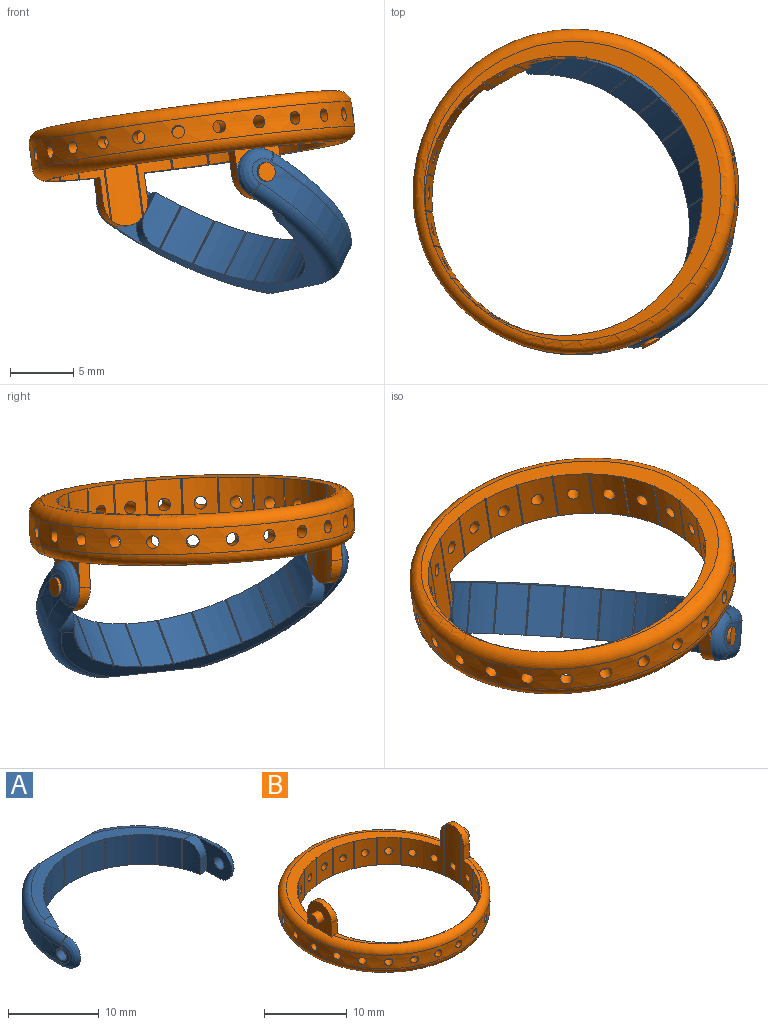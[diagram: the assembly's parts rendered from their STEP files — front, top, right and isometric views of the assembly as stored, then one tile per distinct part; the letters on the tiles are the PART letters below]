
ASSEMBLY  parts=2 mates=1
PART A: 58 faces, bbox 27.8x16x4.1 mm
  f0: cylinder r=12.8mm len=13.16mm, axis (0,0,-1), area 29mm2, adj f7,f51,f52,f53,f54,f55,f57
  f1: cylinder r=12.8mm len=13.16mm, axis (0,0,-1), area 29mm2, adj f7,f46,f47,f48,f49,f50,f56
  f2: plane 1.37x0.02mm, normal (0,0,1), area 0mm2, adj f6,f51
  f3: plane 22.72x8mm, normal (0,0,1), area 37mm2, adj f7,f10,f11,f12,f13,f14,f15,f16
  f4: plane 1.37x0.02mm, normal (0,0,-1), area 0mm2, adj f8,f50
  f5: plane 23.48x10mm, normal (0,0,-1), area 41.1mm2, adj f7,f9,f10,f11,f12,f13,f14,f15
  f6: plane 5.67x4.1mm, normal (-1,0,0), area 13.3mm2, adj f2,f41,f43,f44,f51,f52,f53,f54
  f7: plane 12.39x4mm, normal (0,1,0), area 47.7mm2, adj f0,f1,f3,f5,f46,f50,f51,f52
  f8: plane 5.67x4.1mm, normal (1,0,0), area 13.3mm2, adj f4,f9,f42,f45,f46,f47,f48,f49
  f9: plane 2x0.96mm, normal (0,-1,0), area 1.9mm2, adj f5,f8,f10,f45,f50
  f10: cylinder r=11mm len=4mm, axis (0,0,-1), area 8.1mm2, adj f3,f5,f9,f11,f45
  f11: plane 4x0.09mm, normal (0.78,0.62,0), area 0.5mm2, adj f3,f5,f10,f12
  f12: plane 4x0.11mm, normal (0.12,-0.99,0), area 0.5mm2, adj f3,f5,f11,f13
  f13: cylinder r=11mm len=4mm, axis (0,0,-1), area 11.1mm2, adj f3,f5,f12,f14
  f14: plane 4x0.11mm, normal (0.92,0.4,0), area 0.5mm2, adj f3,f5,f13,f15
  f15: plane 4x0.11mm, normal (-0.15,-0.99,0), area 0.5mm2, adj f3,f5,f14,f16
  f16: cylinder r=11mm len=4mm, axis (0,0,-1), area 11.1mm2, adj f3,f5,f15,f17
  f17: plane 4x0.11mm, normal (0.99,0.15,0), area 0.5mm2, adj f3,f5,f16,f18
  f18: plane 4x0.11mm, normal (-0.4,-0.92,0), area 0.5mm2, adj f3,f5,f17,f19
  f19: cylinder r=11mm len=4mm, axis (0,0,-1), area 11.1mm2, adj f3,f5,f18,f20
  f20: plane 4x0.11mm, normal (0.99,-0.12,0), area 0.5mm2, adj f3,f5,f19,f21
  f21: plane 4x0.09mm, normal (-0.62,-0.78,0), area 0.5mm2, adj f3,f5,f20,f22
  f22: cylinder r=11mm len=4mm, axis (0,0,-1), area 11.1mm2, adj f3,f5,f21,f23
  f23: plane 4x0.11mm, normal (0.93,-0.37,0), area 0.5mm2, adj f3,f5,f22,f24
  f24: plane 4x0.09mm, normal (-0.8,-0.6,0), area 0.5mm2, adj f3,f5,f23,f25
  f25: cylinder r=11mm len=4mm, axis (0,0,-1), area 11.1mm2, adj f3,f5,f24,f26
  f26: plane 4x0.09mm, normal (0.8,-0.6,0), area 0.5mm2, adj f3,f5,f25,f27
  f27: plane 4x0.11mm, normal (-0.93,-0.37,0), area 0.5mm2, adj f3,f5,f26,f28
  f28: cylinder r=11mm len=4mm, axis (0,0,-1), area 11.1mm2, adj f3,f5,f27,f29
  f29: plane 4x0.09mm, normal (0.62,-0.78,0), area 0.5mm2, adj f3,f5,f28,f30
  f30: plane 4x0.11mm, normal (-0.99,-0.12,0), area 0.5mm2, adj f3,f5,f29,f31
  f31: cylinder r=11mm len=4mm, axis (0,0,-1), area 11.1mm2, adj f3,f5,f30,f32
  f32: plane 4x0.11mm, normal (0.4,-0.92,0), area 0.5mm2, adj f3,f5,f31,f33
  f33: plane 4x0.11mm, normal (-0.99,0.15,0), area 0.5mm2, adj f3,f5,f32,f34
  f34: cylinder r=11mm len=4mm, axis (0,0,-1), area 11.1mm2, adj f3,f5,f33,f35
  f35: plane 4x0.11mm, normal (0.15,-0.99,0), area 0.5mm2, adj f3,f5,f34,f36
  f36: plane 4x0.11mm, normal (-0.92,0.4,0), area 0.5mm2, adj f3,f5,f35,f37
  f37: cylinder r=11mm len=4mm, axis (0,0,-1), area 11.1mm2, adj f3,f5,f36,f38
  f38: plane 4x0.11mm, normal (-0.12,-0.99,0), area 0.5mm2, adj f3,f5,f37,f39
  f39: plane 4x0.09mm, normal (-0.78,0.62,0), area 0.5mm2, adj f3,f5,f38,f40
  f40: cylinder r=11mm len=4mm, axis (0,0,-1), area 8.1mm2, adj f3,f5,f39,f41,f44
  f41: plane 2x0.96mm, normal (0,-1,0), area 1.9mm2, adj f5,f6,f40,f44,f52
  f42: plane 1.37x0.02mm, normal (0,0,1), area 0mm2, adj f8,f46
  f43: plane 1.37x0.02mm, normal (0,0,-1), area 0mm2, adj f6,f52
  f44: cylinder r=2mm len=2mm, axis (-1,0,0), area 3.5mm2, adj f3,f6,f40,f41,f51
  f45: cylinder r=2mm len=2mm, axis (-1,0,0), area 3.5mm2, adj f3,f8,f9,f10,f46
  f46: torus R=11.8mm, axis (0,0,1), area 22.7mm2, adj f1,f3,f7,f8,f42,f45,f47
  f47: bspline ~1.12x1.02mm, area 0.2mm2, adj f1,f8,f46,f48
  f48: bspline ~4x2mm, area 7.2mm2, adj f1,f8,f47,f49
  f49: bspline ~1.12x1.02mm, area 0.2mm2, adj f1,f8,f48,f50
  f50: torus R=11.8mm, axis (0,0,1), area 23.1mm2, adj f1,f4,f5,f7,f8,f9,f49
  f51: torus R=11.8mm, axis (0,0,1), area 22.7mm2, adj f0,f2,f3,f6,f7,f44,f53
  f52: torus R=11.8mm, axis (0,0,1), area 23.1mm2, adj f0,f5,f6,f7,f41,f43,f54
  f53: bspline ~1.12x1.02mm, area 0.2mm2, adj f0,f6,f51,f55
  f54: bspline ~1.12x1.02mm, area 0.2mm2, adj f0,f6,f52,f55
  f55: bspline ~4x2mm, area 7.2mm2, adj f0,f6,f53,f54
  f56: cylinder r=0.75mm len=1.5mm, axis (1,0,0), area 4.6mm2, adj f1,f8
  f57: cylinder r=0.75mm len=1.5mm, axis (1,0,0), area 4.6mm2, adj f0,f6
PART B: 125 faces, bbox 27.7x27.7x8 mm
  f0: plane 2.72x0.72mm, normal (0,0,1), area 0.1mm2, adj f44,f45,f46,f124
  f1: plane 8.21x7.21mm, normal (0,0,1), area 3.4mm2, adj f33,f34,f35,f36,f37,f38,f39,f40
  f2: plane 1.37x0.02mm, normal (0,0,1), area 0mm2, adj f112,f124
  f3: plane 23.48x10.6mm, normal (0,0,1), area 44.1mm2, adj f12,f13,f14,f15,f16,f17,f18,f19
  f4: plane 1.37x0.02mm, normal (0,0,1), area 0mm2, adj f115,f124
  f5: plane 8.21x7.21mm, normal (0,0,1), area 3.4mm2, adj f53,f54,f55,f56,f57,f58,f59,f60
  f6: plane 2.72x0.72mm, normal (0,0,1), area 0.1mm2, adj f50,f51,f52,f124
  f7: plane 1.38x0.09mm, normal (0,0,1), area 0mm2, adj f48,f49,f124
  f8: plane 1.38x0.09mm, normal (0,0,-1), area 0mm2, adj f47,f48,f123
  f9: plane 1.38x0.09mm, normal (0,0,-1), area 0mm2, adj f48,f49,f123
  f10: plane 2.72x0.72mm, normal (0,0,-1), area 0.1mm2, adj f50,f51,f52,f123
  f11: plane 23.6x22.81mm, normal (0,0,-1), area 57mm2, adj f12,f13,f14,f15,f16,f17,f18,f19
  f12: cylinder r=11mm len=4mm, axis (0,0,-1), area 10.3mm2, adj f3,f11,f13,f84,f87
  f13: plane 4x0.09mm, normal (0.8,-0.6,0), area 0.5mm2, adj f3,f11,f12,f14
  f14: plane 4x0.11mm, normal (-0.93,-0.37,0), area 0.5mm2, adj f3,f11,f13,f15
  f15: cylinder r=11mm len=4mm, axis (0,0,-1), area 10.3mm2, adj f3,f11,f14,f16,f94
  f16: plane 4x0.09mm, normal (0.62,-0.78,0), area 0.5mm2, adj f3,f11,f15,f17
  f17: plane 4x0.11mm, normal (-0.99,-0.12,0), area 0.5mm2, adj f3,f11,f16,f18
  f18: cylinder r=11mm len=4mm, axis (0,0,-1), area 10.3mm2, adj f3,f11,f17,f19,f92
  f19: plane 4x0.11mm, normal (0.4,-0.92,0), area 0.5mm2, adj f3,f11,f18,f20
  f20: plane 4x0.11mm, normal (-0.99,0.15,0), area 0.5mm2, adj f3,f11,f19,f21
  f21: cylinder r=11mm len=4mm, axis (0,0,-1), area 10.3mm2, adj f3,f11,f20,f22,f93
  f22: plane 4x0.11mm, normal (0.15,-0.99,0), area 0.5mm2, adj f3,f11,f21,f23
  f23: plane 4x0.11mm, normal (-0.92,0.4,0), area 0.5mm2, adj f3,f11,f22,f24
  f24: cylinder r=11mm len=4mm, axis (0,0,-1), area 10.3mm2, adj f3,f11,f23,f25,f91
  f25: plane 4x0.11mm, normal (-0.12,-0.99,0), area 0.5mm2, adj f3,f11,f24,f26
  f26: plane 4x0.09mm, normal (-0.78,0.62,0), area 0.5mm2, adj f3,f11,f25,f27
  f27: cylinder r=11mm len=7.33mm, axis (0,0,-1), area 11.8mm2, adj f3,f11,f26,f28,f90,f113,f121
  f28: plane 7.38x0.11mm, normal (-0.37,-0.93,0), area 0.8mm2, adj f11,f27,f29,f121
  f29: plane 7.45x0.09mm, normal (-0.6,0.8,0), area 0.9mm2, adj f11,f28,f30,f121
  f30: cylinder r=11mm len=8mm, axis (0,0,-1), area 20.9mm2, adj f11,f29,f31,f89,f121
  f31: plane 7.45x0.09mm, normal (-0.6,-0.8,0), area 0.9mm2, adj f11,f30,f32,f121
  f32: plane 7.38x0.11mm, normal (-0.37,0.93,0), area 0.8mm2, adj f11,f31,f33,f121
  f33: cylinder r=11mm len=7.33mm, axis (0,0,-1), area 11.8mm2, adj f1,f11,f32,f34,f88,f111,f121
  f34: plane 4x0.09mm, normal (-0.78,-0.62,0), area 0.5mm2, adj f1,f11,f33,f35
  f35: plane 4x0.11mm, normal (-0.12,0.99,0), area 0.5mm2, adj f1,f11,f34,f36
  f36: cylinder r=11mm len=4mm, axis (0,0,-1), area 10.3mm2, adj f1,f11,f35,f37,f108
  f37: plane 4x0.11mm, normal (-0.92,-0.4,0), area 0.5mm2, adj f1,f11,f36,f38
  f38: plane 4x0.11mm, normal (0.15,0.99,0), area 0.5mm2, adj f1,f11,f37,f39
  f39: cylinder r=11mm len=4mm, axis (0,0,-1), area 10.3mm2, adj f1,f11,f38,f40,f107
  f40: plane 4x0.11mm, normal (-0.99,-0.15,0), area 0.5mm2, adj f1,f11,f39,f41
  f41: plane 4x0.11mm, normal (0.4,0.92,0), area 0.5mm2, adj f1,f11,f40,f42
  f42: cylinder r=11mm len=4mm, axis (0,0,-1), area 10.3mm2, adj f1,f11,f41,f43,f109
  f43: plane 4x0.11mm, normal (-0.99,0.12,0), area 0.5mm2, adj f1,f11,f42,f44,f123,f124
  f44: plane 4x0.09mm, normal (0.62,0.78,0), area 0.5mm2, adj f0,f43,f45,f86,f123,f124
  f45: cylinder r=11mm len=4mm, axis (0,0,-1), area 10.3mm2, adj f0,f44,f46,f86,f110
  f46: plane 4x0.11mm, normal (-0.93,0.37,0), area 0.5mm2, adj f0,f45,f47,f86,f123,f124
  f47: plane 4x0.09mm, normal (0.8,0.6,0), area 0.5mm2, adj f8,f46,f48,f85,f123,f124
  f48: cylinder r=11mm len=4mm, axis (0,0,-1), area 10.3mm2, adj f7,f8,f9,f47,f49,f85,f106
  f49: plane 4x0.09mm, normal (-0.8,0.6,0), area 0.5mm2, adj f7,f9,f48,f50,f123,f124
  f50: plane 4x0.11mm, normal (0.93,0.37,0), area 0.5mm2, adj f6,f10,f49,f51,f123,f124
  f51: cylinder r=11mm len=4mm, axis (0,0,-1), area 10.3mm2, adj f6,f10,f50,f52,f105
  f52: plane 4x0.09mm, normal (-0.62,0.78,0), area 0.5mm2, adj f6,f10,f51,f53,f123,f124
  f53: plane 4x0.11mm, normal (0.99,0.12,0), area 0.5mm2, adj f5,f11,f52,f54,f123,f124
  f54: cylinder r=11mm len=4mm, axis (0,0,-1), area 10.3mm2, adj f5,f11,f53,f55,f103
  f55: plane 4x0.11mm, normal (-0.4,0.92,0), area 0.5mm2, adj f5,f11,f54,f56
  f56: plane 4x0.11mm, normal (0.99,-0.15,0), area 0.5mm2, adj f5,f11,f55,f57
  f57: cylinder r=11mm len=4mm, axis (0,0,-1), area 10.3mm2, adj f5,f11,f56,f58,f104
  f58: plane 4x0.11mm, normal (-0.15,0.99,0), area 0.5mm2, adj f5,f11,f57,f59
  f59: plane 4x0.11mm, normal (0.92,-0.4,0), area 0.5mm2, adj f5,f11,f58,f60
  f60: cylinder r=11mm len=4mm, axis (0,0,-1), area 10.3mm2, adj f5,f11,f59,f61,f102
  f61: plane 4x0.11mm, normal (0.12,0.99,0), area 0.5mm2, adj f5,f11,f60,f62
  f62: plane 4x0.09mm, normal (0.78,-0.62,0), area 0.5mm2, adj f5,f11,f61,f63
  f63: cylinder r=11mm len=7.33mm, axis (0,0,-1), area 11.8mm2, adj f5,f11,f62,f64,f101,f116,f122
  f64: plane 7.38x0.11mm, normal (0.37,0.93,0), area 0.8mm2, adj f11,f63,f65,f122
  f65: plane 7.45x0.09mm, normal (0.6,-0.8,0), area 0.9mm2, adj f11,f64,f66,f122
  f66: cylinder r=11mm len=8mm, axis (0,0,-1), area 20.9mm2, adj f11,f65,f67,f100,f122
  f67: plane 7.45x0.09mm, normal (0.6,0.8,0), area 0.9mm2, adj f11,f66,f68,f122
  f68: plane 7.38x0.11mm, normal (0.37,-0.93,0), area 0.8mm2, adj f11,f67,f69,f122
  f69: cylinder r=11mm len=7.33mm, axis (0,0,-1), area 11.8mm2, adj f3,f11,f68,f70,f99,f114,f122
  f70: plane 4x0.09mm, normal (0.78,0.62,0), area 0.5mm2, adj f3,f11,f69,f71
  f71: plane 4x0.11mm, normal (0.12,-0.99,0), area 0.5mm2, adj f3,f11,f70,f72
  f72: cylinder r=11mm len=4mm, axis (0,0,-1), area 10.3mm2, adj f3,f11,f71,f73,f96
  f73: plane 4x0.11mm, normal (0.92,0.4,0), area 0.5mm2, adj f3,f11,f72,f74
  f74: plane 4x0.11mm, normal (-0.15,-0.99,0), area 0.5mm2, adj f3,f11,f73,f75
  f75: cylinder r=11mm len=4mm, axis (0,0,-1), area 10.3mm2, adj f3,f11,f74,f76,f95
  f76: plane 4x0.11mm, normal (0.99,0.15,0), area 0.5mm2, adj f3,f11,f75,f77
  f77: plane 4x0.11mm, normal (-0.4,-0.92,0), area 0.5mm2, adj f3,f11,f76,f78
  f78: cylinder r=11mm len=4mm, axis (0,0,-1), area 10.3mm2, adj f3,f11,f77,f79,f97
  f79: plane 4x0.11mm, normal (0.99,-0.12,0), area 0.5mm2, adj f3,f11,f78,f80
  f80: plane 4x0.09mm, normal (-0.62,-0.78,0), area 0.5mm2, adj f3,f11,f79,f81
  f81: cylinder r=11mm len=4mm, axis (0,0,-1), area 10.3mm2, adj f3,f11,f80,f82,f98
  f82: plane 4x0.11mm, normal (0.93,-0.37,0), area 0.5mm2, adj f3,f11,f81,f84
  f83: cylinder r=12.8mm len=25.6mm, axis (0,0,-1), area 142mm2, adj f87,f88,f89,f90,f91,f92,f93,f94
  f84: plane 4x0.09mm, normal (-0.8,-0.6,0), area 0.5mm2, adj f3,f11,f12,f82
  f85: plane 1.38x0.09mm, normal (0,0,1), area 0mm2, adj f47,f48,f124
  f86: plane 2.72x0.72mm, normal (0,0,-1), area 0.1mm2, adj f44,f45,f46,f123
  f87: cylinder r=0.5mm len=2.6mm, axis (0,-1,0), area 8.2mm2, adj f12,f83
  f88: cylinder r=0.5mm len=1.79mm, axis (-0.97,0.26,0), area 4.9mm2, adj f33,f83
  f89: cylinder r=0.5mm len=1.8mm, axis (-1,0,0), area 5.6mm2, adj f30,f83
  f90: cylinder r=0.5mm len=2.19mm, axis (-0.97,-0.26,0), area 6.2mm2, adj f27,f83
  f91: cylinder r=0.5mm len=2.4mm, axis (-0.87,-0.5,0), area 6.8mm2, adj f24,f83
  f92: cylinder r=0.5mm len=2.66mm, axis (-0.5,-0.87,0), area 7.8mm2, adj f18,f83
  f93: cylinder r=0.5mm len=2.38mm, axis (-0.71,-0.71,0), area 7.4mm2, adj f21,f83
  f94: cylinder r=0.5mm len=2.74mm, axis (-0.26,-0.97,0), area 8.1mm2, adj f15,f83
  f95: cylinder r=0.5mm len=2.38mm, axis (0.71,-0.71,0), area 7.4mm2, adj f75,f83
  f96: cylinder r=0.5mm len=2.4mm, axis (0.87,-0.5,0), area 6.8mm2, adj f72,f83
  f97: cylinder r=0.5mm len=2.66mm, axis (0.5,-0.87,0), area 7.8mm2, adj f78,f83
  f98: cylinder r=0.5mm len=2.74mm, axis (0.26,-0.97,0), area 8.1mm2, adj f81,f83
  f99: cylinder r=0.5mm len=2.19mm, axis (0.97,-0.26,0), area 6.2mm2, adj f69,f83
  f100: cylinder r=0.5mm len=1.8mm, axis (1,0,0), area 5.6mm2, adj f66,f83
  f101: cylinder r=0.5mm len=1.79mm, axis (0.97,0.26,0), area 4.9mm2, adj f63,f83
  f102: cylinder r=0.5mm len=1.71mm, axis (0.87,0.5,0), area 4.3mm2, adj f60,f83
  f103: cylinder r=0.5mm len=1.46mm, axis (0.5,0.87,0), area 3.4mm2, adj f54,f83
  f104: cylinder r=0.5mm len=1.58mm, axis (0.71,0.71,0), area 3.8mm2, adj f57,f83
  f105: cylinder r=0.5mm len=1.25mm, axis (0.26,0.97,0), area 3.2mm2, adj f51,f83
  f106: cylinder r=0.5mm len=1mm, axis (0,1,0), area 3.1mm2, adj f48,f83
  f107: cylinder r=0.5mm len=1.58mm, axis (-0.71,0.71,0), area 3.8mm2, adj f39,f83
  f108: cylinder r=0.5mm len=1.71mm, axis (-0.87,0.5,0), area 4.3mm2, adj f36,f83
  f109: cylinder r=0.5mm len=1.46mm, axis (-0.5,0.87,0), area 3.4mm2, adj f42,f83
  f110: cylinder r=0.5mm len=1.25mm, axis (-0.26,0.97,0), area 3.2mm2, adj f45,f83
  f111: plane 2.05x0.97mm, normal (0,-1,0), area 1.9mm2, adj f1,f33,f112,f121,f124
  f112: plane 4.05x4.01mm, normal (1,0,0), area 12.5mm2, adj f2,f111,f113,f117,f121,f124
  f113: plane 2x0.96mm, normal (0,1,0), area 1.9mm2, adj f3,f27,f112,f121,f124
  f114: plane 2x0.96mm, normal (0,1,0), area 1.9mm2, adj f3,f69,f115,f122,f124
  f115: plane 4.05x4.01mm, normal (-1,0,0), area 12.5mm2, adj f4,f114,f116,f119,f122,f124
  f116: plane 2.05x0.97mm, normal (0,-1,0), area 1.9mm2, adj f5,f63,f115,f122,f124
  f117: cylinder r=0.75mm len=1.5mm, axis (-1,0,0), area 5.7mm2, adj f112,f118
  f118: plane 1.5x1.5mm, normal (1,0,0), area 1.8mm2, adj f117
  f119: cylinder r=0.75mm len=1.5mm, axis (1,0,0), area 5.7mm2, adj f115,f120
  f120: plane 1.5x1.5mm, normal (-1,0,0), area 1.8mm2, adj f119
  f121: cylinder r=2mm len=4mm, axis (-1,0,0), area 5.5mm2, adj f27,f28,f29,f30,f31,f32,f33,f111
  f122: cylinder r=2mm len=4mm, axis (-1,0,0), area 5.5mm2, adj f63,f64,f65,f66,f67,f68,f69,f114
  f123: torus R=11.8mm, axis (0,0,1), area 122.7mm2, adj f8,f9,f10,f11,f43,f44,f46,f47
  f124: torus R=11.8mm, axis (0,0,1), area 122.2mm2, adj f0,f1,f2,f3,f4,f5,f6,f7
PLACE A rot(axis=(-0.51,-0.82,0.26),168.4deg) t=(-15.9,-0.18,3.16)mm
PLACE B rot(axis=(0.51,0.86,0.02),172.5deg) t=(-18.12,-1.3,3.73)mm
MATE revolute A.f56 <-> B.f119  axis (-0.47,0.88,-0.09) through (-12.07,-11.8,0.88)mm
